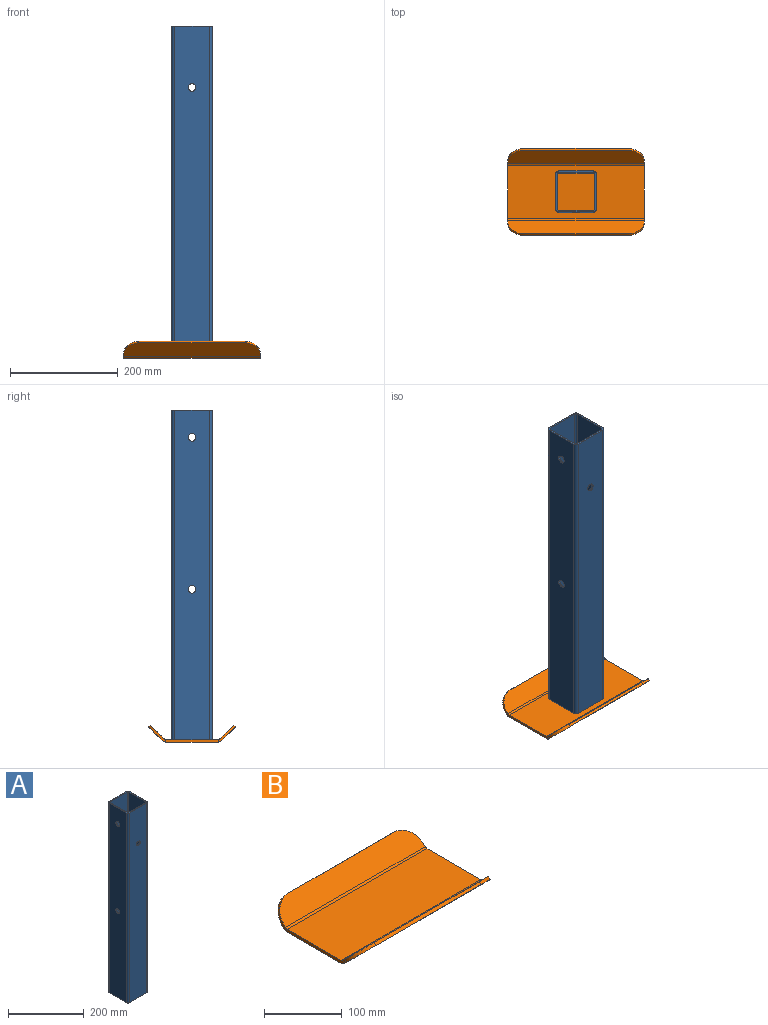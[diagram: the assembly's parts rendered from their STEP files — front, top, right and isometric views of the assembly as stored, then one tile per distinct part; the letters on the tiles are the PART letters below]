
ASSEMBLY  parts=2 mates=1
PART A: 24 faces, bbox 76.2x76.2x612.8 mm
  f0: cylinder r=3.3mm len=612.78mm, axis (0,0,-1), area 3178.3mm2, adj f1,f15,f16,f17
  f1: plane 612.78x63.5mm, normal (-1,0,0), area 38590.6mm2, adj f0,f2,f16,f17,f22,f23
  f2: cylinder r=3.3mm len=612.78mm, axis (0,0,-1), area 3178.3mm2, adj f1,f3,f16,f17
  f3: plane 612.78x63.5mm, normal (0,1,0), area 38750.9mm2, adj f2,f4,f16,f17,f19
  f4: cylinder r=3.3mm len=612.78mm, axis (0,0,-1), area 3178.3mm2, adj f3,f5,f16,f17
  f5: plane 612.78x63.5mm, normal (1,0,0), area 38590.6mm2, adj f4,f6,f16,f17,f20,f21
  f6: cylinder r=3.3mm len=612.78mm, axis (0,0,-1), area 3178.3mm2, adj f5,f15,f16,f17
  f7: plane 612.78x63.5mm, normal (1,0,0), area 38590.6mm2, adj f8,f14,f16,f17,f22,f23
  f8: cylinder r=6.35mm len=612.78mm, axis (0,0,-1), area 6112.2mm2, adj f7,f9,f16,f17
  f9: plane 612.78x63.5mm, normal (0,1,0), area 38750.9mm2, adj f8,f10,f16,f17,f18
  f10: cylinder r=6.35mm len=612.78mm, axis (0,0,-1), area 6112.2mm2, adj f9,f11,f16,f17
  f11: plane 612.78x63.5mm, normal (-1,0,0), area 38590.6mm2, adj f10,f12,f16,f17,f20,f21
  f12: cylinder r=6.35mm len=612.78mm, axis (0,0,-1), area 6112.2mm2, adj f11,f13,f16,f17
  f13: plane 612.78x63.5mm, normal (0,-1,0), area 38750.9mm2, adj f12,f14,f16,f17,f19
  f14: cylinder r=6.35mm len=612.78mm, axis (0,0,-1), area 6112.2mm2, adj f7,f13,f16,f17
  f15: plane 612.78x63.5mm, normal (0,-1,0), area 38750.9mm2, adj f0,f6,f16,f17,f18
  f16: plane 76.2x76.2mm, normal (0,0,1), area 866.6mm2, adj f0,f1,f2,f3,f4,f5,f6,f7
  f17: plane 76.2x76.2mm, normal (0,0,-1), area 866.6mm2, adj f0,f1,f2,f3,f4,f5,f6,f7
  f18: cylinder r=7.14mm len=14.29mm, axis (0,-1,0), area 136.8mm2, adj f9,f15
  f19: cylinder r=7.14mm len=14.29mm, axis (0,-1,0), area 136.8mm2, adj f3,f13
  f20: cylinder r=7.14mm len=14.29mm, axis (1,0,0), area 136.8mm2, adj f5,f11
  f21: cylinder r=7.14mm len=14.29mm, axis (1,0,0), area 136.8mm2, adj f5,f11
  f22: cylinder r=7.14mm len=14.29mm, axis (1,0,0), area 136.8mm2, adj f1,f7
  f23: cylinder r=7.14mm len=14.29mm, axis (1,0,0), area 136.8mm2, adj f1,f7
PART B: 26 faces, bbox 254x162x31.6 mm
  f0: plane 97.65x4.55mm, normal (-1,0,0), area 444mm2, adj f2,f3,f12,f23
  f1: plane 97.65x4.55mm, normal (1,0,0), area 444mm2, adj f2,f3,f11,f22
  f2: plane 254x97.65mm, normal (0,0,-1), area 24804.3mm2, adj f0,f1,f13,f24
  f3: plane 254x97.65mm, normal (0,0,1), area 24804.3mm2, adj f0,f1,f14,f25
  f4: plane 6.38x6.38mm, normal (-1,0,0), area 20.3mm2, adj f7,f8,f9,f12
  f5: plane 190.5x3.22mm, normal (0,0.71,0.71), area 866.1mm2, adj f7,f8,f9,f10
  f6: plane 6.38x6.38mm, normal (1,0,0), area 20.3mm2, adj f7,f8,f10,f11
  f7: plane 254x25.61mm, normal (0,0.71,-0.71), area 8767.6mm2, adj f4,f5,f6,f9,f10,f13
  f8: plane 254x25.61mm, normal (0,-0.71,0.71), area 8767.6mm2, adj f4,f5,f6,f9,f10,f14
  f9: cylinder r=31.75mm len=31.75mm, axis (0,-0.71,0.71), area 226.8mm2, adj f4,f5,f7,f8
  f10: cylinder r=31.75mm len=31.75mm, axis (0,0.71,-0.71), area 226.8mm2, adj f5,f6,f7,f8
  f11: plane 6.58x5.94mm, normal (1,0,0), area 25.1mm2, adj f1,f6,f13,f14
  f12: plane 6.58x5.94mm, normal (-1,0,0), area 25.1mm2, adj f0,f4,f13,f14
  f13: cylinder r=9.31mm len=254mm, axis (1,0,0), area 1857.1mm2, adj f2,f7,f11,f12
  f14: cylinder r=4.76mm len=254mm, axis (1,0,0), area 950.1mm2, adj f3,f8,f11,f12
  f15: plane 6.38x6.38mm, normal (-1,0,0), area 20.3mm2, adj f18,f19,f21,f23
  f16: plane 6.38x6.38mm, normal (1,0,0), area 20.3mm2, adj f18,f19,f20,f22
  f17: plane 190.5x3.22mm, normal (0,-0.71,0.71), area 866.1mm2, adj f18,f19,f20,f21
  f18: plane 254x25.61mm, normal (0,-0.71,-0.71), area 8767.6mm2, adj f15,f16,f17,f20,f21,f24
  f19: plane 254x25.61mm, normal (0,0.71,0.71), area 8767.6mm2, adj f15,f16,f17,f20,f21,f25
  f20: cylinder r=31.75mm len=31.75mm, axis (0,-0.71,-0.71), area 226.8mm2, adj f16,f17,f18,f19
  f21: cylinder r=31.75mm len=31.75mm, axis (0,0.71,0.71), area 226.8mm2, adj f15,f17,f18,f19
  f22: plane 6.58x5.94mm, normal (1,0,0), area 25.1mm2, adj f1,f16,f24,f25
  f23: plane 6.58x5.94mm, normal (-1,0,0), area 25.1mm2, adj f0,f15,f24,f25
  f24: cylinder r=9.31mm len=254mm, axis (1,0,0), area 1857.1mm2, adj f2,f18,f22,f23
  f25: cylinder r=4.76mm len=254mm, axis (1,0,0), area 950.1mm2, adj f3,f19,f22,f23
PLACE A t=(-257.06,-172.88,498.07)mm
PLACE B t=(-130.06,-172.88,191.68)mm
MATE planar B.f3 <-> A.f17  axis (0,0,1) through (-257.06,-172.88,191.68)mm
